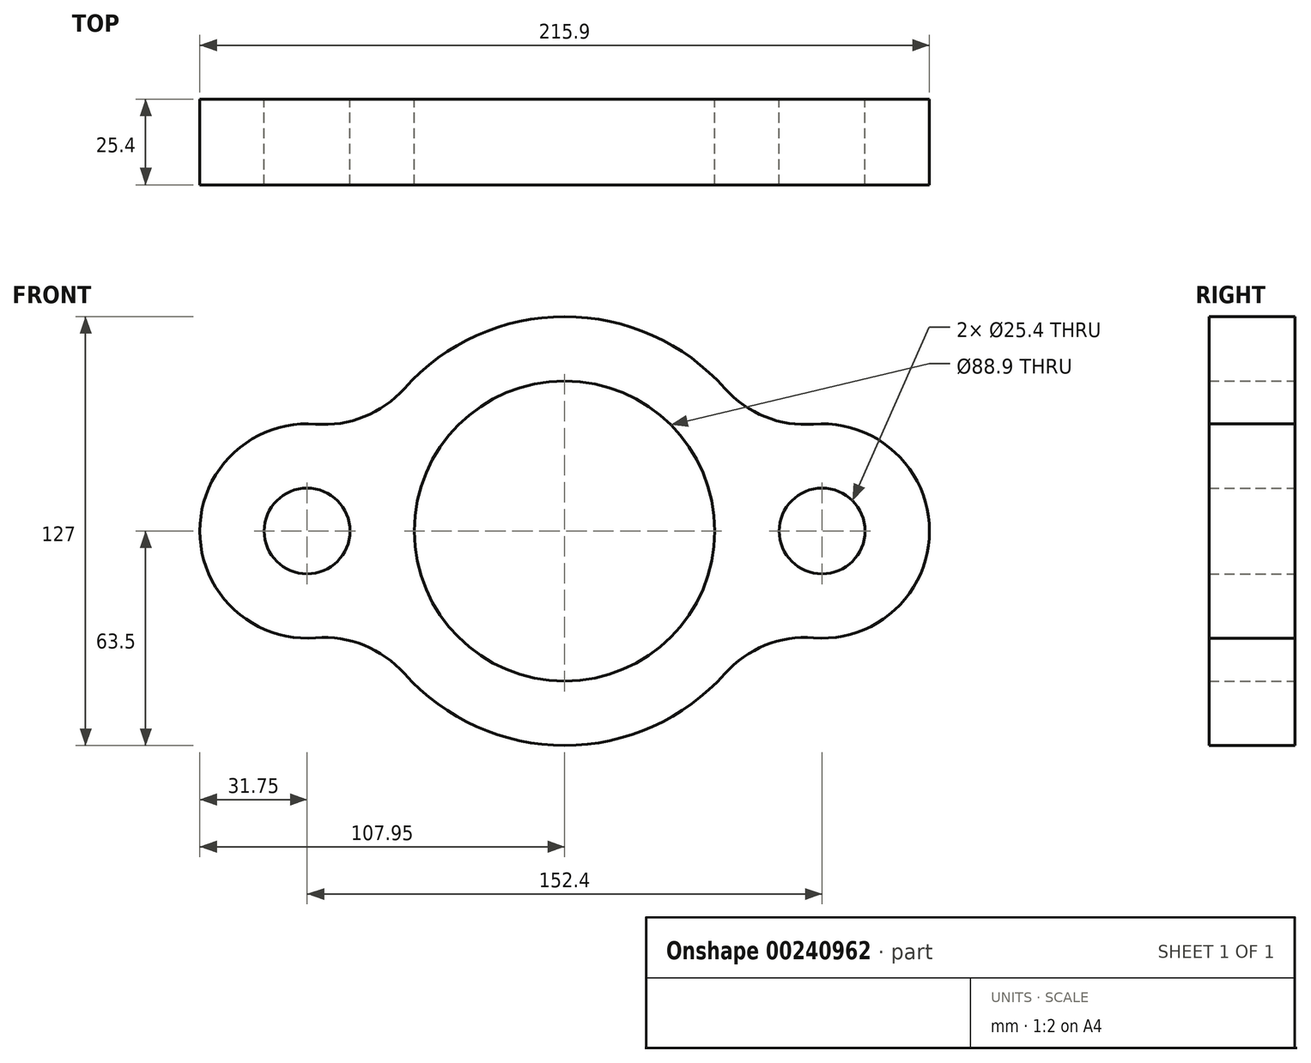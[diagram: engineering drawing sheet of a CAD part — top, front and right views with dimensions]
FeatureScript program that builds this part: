
annotation { "Feature Type Name" : "Feature", "Feature Type Description" : "" }
export const myFeature = defineFeature(function(context is Context, id is Id, definition is map)
    precondition{}
    {
        {
            var Q0;
            Q0=qCreatedBy(makeId("Front.planeOp"),FACE);
            var sketch = newSketch(context, id + "F0", { "sketchPlane" : qUnion([Q0])});
            skCircle(sketch, "E0", {"center": v(0, 0) * mm, "radius": 44.45 * mm});
            skArc(sketch, "E1", {"start": v(-47.45, -42.2) * mm, "mid": v(0, -63.5) * mm, "end": v(47.45, -42.2) * mm});
            skLineSegment(sketch, "E2", {"start": v(0, 0) * mm, "end": v(-97.86, 0) * mm, "construction": true});
            skLineSegment(sketch, "E3", {"start": v(0, 0) * mm, "end": v(113.98, 0) * mm, "construction": true});
            skCircle(sketch, "E4", {"center": v(-76.2, 0) * mm, "radius": 12.7 * mm});
            skArc(sketch, "E5", {"start": v(-73.69, 31.65) * mm, "mid": v(-107.95, 0) * mm, "end": v(-73.69, -31.65) * mm});
            skLineSegment(sketch, "E6", {"start": v(0, 0) * mm, "end": v(0, 40.1) * mm});
            skArc(sketch, "E7.MirrorC", {"start": v(73.69, 31.65) * mm, "mid": v(107.95, 0) * mm, "end": v(73.69, -31.65) * mm});
            skCircle(sketch, "E8.MirrorC", {"center": v(76.2, 0) * mm, "radius": 12.7 * mm});
            skArc(sketch, "E9", {"start": v(-73.69, 31.65) * mm, "mid": v(-59.33, 33.84) * mm, "end": v(-47.45, 42.2) * mm});
            skArc(sketch, "E10", {"start": v(47.45, 42.2) * mm, "mid": v(59.33, 33.84) * mm, "end": v(73.69, 31.65) * mm});
            skArc(sketch, "E11.MirrorC", {"start": v(47.45, -42.2) * mm, "mid": v(59.33, -33.84) * mm, "end": v(73.69, -31.65) * mm});
            skArc(sketch, "E12.MirrorC", {"start": v(-47.45, 42.2) * mm, "mid": v(0, 63.5) * mm, "end": v(47.45, 42.2) * mm});
            skArc(sketch, "E13.MirrorC", {"start": v(-73.69, -31.65) * mm, "mid": v(-59.33, -33.84) * mm, "end": v(-47.45, -42.2) * mm});
            skArc(sketch, "E14.trimOffspring", {"start": v(47.45, 42.2) * mm, "mid": v(0, 63.5) * mm, "end": v(-47.45, 42.2) * mm});
            skArc(sketch, "E15.trimOffspring", {"start": v(47.45, -42.2) * mm, "mid": v(0, -63.5) * mm, "end": v(-47.45, -42.2) * mm});
            skArc(sketch, "E16.trimOffspring", {"start": v(73.69, -31.65) * mm, "mid": v(107.95, 0) * mm, "end": v(73.69, 31.65) * mm});
            skSolve(sketch);
        }
        {
            var Q0;
            Q0=makeQuery(id+"F0.imprint","IMPRINT",FACE,{"disambiguationData":[TD([[makeQuery(id+"F0.imprint","IMPRINT",EDGE,{"derivedFrom":sQuery(id+"F0.wireOp",EDGE,"E4")}),-1.0]])]});
            extrude(context, id + "F1", {"entities" : qUnion([Q0]), "depth" : 25.4 * mm});
        }
    });
